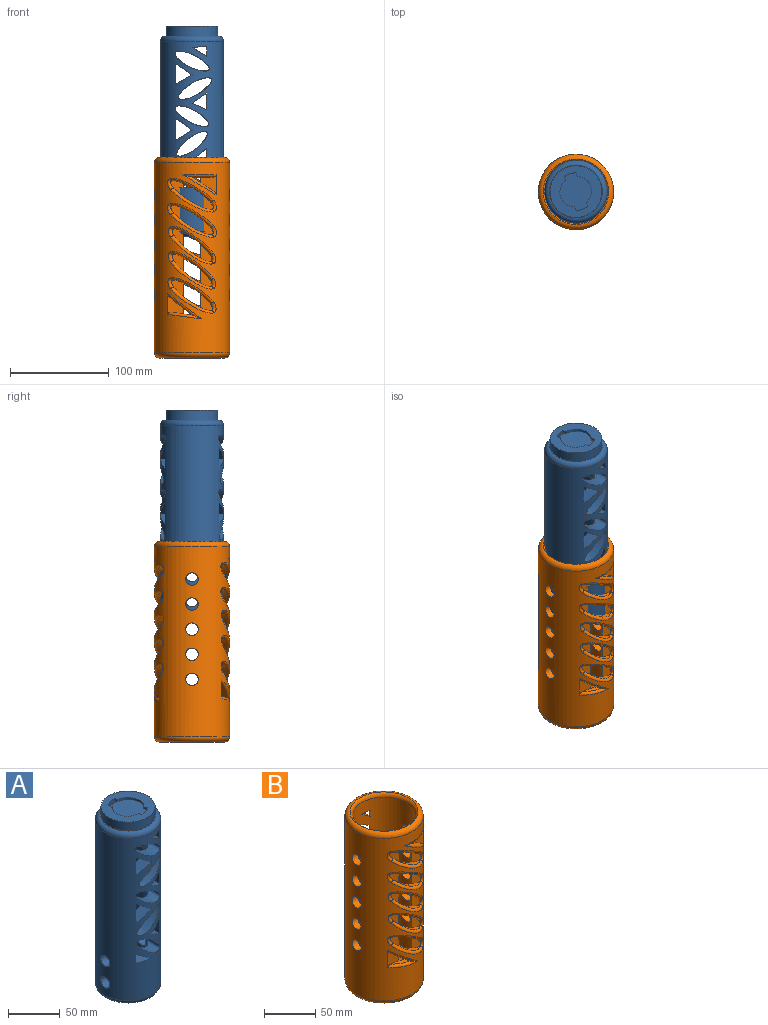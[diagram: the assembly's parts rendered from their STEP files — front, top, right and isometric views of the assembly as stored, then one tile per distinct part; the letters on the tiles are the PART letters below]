
ASSEMBLY  parts=2 mates=1
PART A: 68 faces, bbox 69x69x213.6 mm
  f0: cylinder r=31.75mm len=193.04mm, axis (0,0,-1), area 32342.8mm2, adj f4,f5,f6,f7,f8,f9,f10,f11
  f1: cylinder r=19.05mm len=203.2mm, axis (0,0,1), area 17379.8mm2, adj f3,f6,f7,f8,f9,f10,f11,f12
  f2: plane 53.34x53.34mm, normal (0,0,1), area 75.9mm2, adj f5,f56
  f3: plane 53.34x53.34mm, normal (0,0,-1), area 1094.5mm2, adj f1,f4
  f4: torus R=26.67mm, axis (0,0,1), area 1499.3mm2, adj f0,f3
  f5: torus R=26.67mm, axis (0,0,1), area 1499.3mm2, adj f0,f2
  f6: cylinder r=6.35mm len=13.79mm, axis (1,0,0), area 515.5mm2, adj f0,f1
  f7: cylinder r=6.35mm len=13.79mm, axis (1,0,0), area 515.5mm2, adj f0,f1
  f8: cylinder r=6.35mm len=13.79mm, axis (1,0,0), area 515.5mm2, adj f0,f1
  f9: cylinder r=6.35mm len=13.79mm, axis (1,0,0), area 515.5mm2, adj f0,f1
  f10: extruded ~31.64x24.69mm, area 1200.9mm2, adj f0,f1
  f11: extruded ~31.64x24.69mm, area 1200.7mm2, adj f0,f1
  f12: plane 22.21x16.49mm, normal (0,0,1), area 230.4mm2, adj f0,f1,f13,f14
  f13: plane 17.59x10.4mm, normal (1,0,0), area 182.9mm2, adj f0,f1,f12,f14
  f14: plane 22.21x16.49mm, normal (-0.53,0,-0.85), area 272.4mm2, adj f0,f1,f12,f13
  f15: plane 22.21x16.49mm, normal (-0.53,0,-0.85), area 272.4mm2, adj f0,f1,f16,f17
  f16: plane 17.59x10.4mm, normal (1,0,0), area 182.9mm2, adj f0,f1,f15,f17
  f17: plane 22.21x16.49mm, normal (0,0,1), area 230.4mm2, adj f0,f1,f15,f16
  f18: plane 19.93x14.94mm, normal (0.53,0,0.85), area 241.2mm2, adj f0,f1,f19,f20
  f19: plane 19.99x15mm, normal (0.03,0,-1), area 204.5mm2, adj f0,f1,f18,f20
  f20: plane 16.2x9.88mm, normal (-1,0,0), area 160mm2, adj f0,f1,f18,f19
  f21: plane 16.2x9.88mm, normal (-1,0,0), area 160mm2, adj f0,f1,f22,f23
  f22: plane 19.99x15mm, normal (0.03,0,-1), area 204.5mm2, adj f0,f1,f21,f23
  f23: plane 19.93x14.94mm, normal (0.53,0,0.85), area 241.2mm2, adj f0,f1,f21,f22
  f24: extruded ~31.09x25.36mm, area 1192.9mm2, adj f0,f1
  f25: extruded ~31.09x25.36mm, area 1192.9mm2, adj f0,f1
  f26: extruded ~33.98x23.15mm, area 1226.3mm2, adj f0,f1
  f27: extruded ~33.98x23.15mm, area 1226.7mm2, adj f0,f1
  f28: extruded ~63.5x33.44mm, area 2541.8mm2, adj f0,f1
  f29: extruded ~34.6x23.8mm, area 1230.5mm2, adj f0,f1
  f30: extruded ~34.6x23.8mm, area 1230.1mm2, adj f0,f1
  f31: plane 22.21x16.49mm, normal (-0.53,0,0.85), area 272mm2, adj f0,f1,f32,f33
  f32: plane 22.68x17.59mm, normal (1,0,0), area 398.9mm2, adj f0,f1,f31,f33
  f33: plane 22.21x16.49mm, normal (-0.6,0,-0.8), area 287.8mm2, adj f0,f1,f31,f32
  f34: plane 22.21x16.49mm, normal (-0.6,0,-0.8), area 287.8mm2, adj f0,f1,f35,f36
  f35: plane 22.68x17.59mm, normal (1,0,0), area 398.9mm2, adj f0,f1,f34,f36
  f36: plane 22.21x16.49mm, normal (-0.53,0,0.85), area 272mm2, adj f0,f1,f34,f35
  f37: plane 20.2x15.21mm, normal (0.49,0,0.87), area 234.2mm2, adj f0,f1,f38,f39
  f38: plane 19.93x14.94mm, normal (0.61,0,-0.79), area 258.2mm2, adj f0,f1,f37,f39
  f39: plane 19.89x16.2mm, normal (-1,0,0), area 322.2mm2, adj f0,f1,f37,f38
  f40: plane 19.89x16.2mm, normal (-1,0,0), area 322.2mm2, adj f0,f1,f41,f42
  f41: plane 19.93x14.94mm, normal (0.61,0,-0.79), area 258.2mm2, adj f0,f1,f40,f42
  f42: plane 20.2x15.21mm, normal (0.49,0,0.87), area 234.2mm2, adj f0,f1,f40,f41
  f43: plane 20.15x15.16mm, normal (0.41,0,0.91), area 224.3mm2, adj f0,f1,f44,f45
  f44: plane 19.93x14.94mm, normal (0.57,0,-0.82), area 248.6mm2, adj f0,f1,f43,f45
  f45: plane 17.11x16.2mm, normal (-1,0,0), area 277.1mm2, adj f0,f1,f43,f44
  f46: plane 17.11x16.2mm, normal (-1,0,0), area 277.1mm2, adj f0,f1,f47,f48
  f47: plane 19.93x14.94mm, normal (0.57,0,-0.82), area 248.6mm2, adj f0,f1,f46,f48
  f48: plane 20.15x15.16mm, normal (0.41,0,0.91), area 224.3mm2, adj f0,f1,f46,f47
  f49: plane 22.21x16.49mm, normal (-0.5,0,0.87), area 266.3mm2, adj f0,f1,f50,f51
  f50: plane 21.09x17.59mm, normal (1,0,0), area 371mm2, adj f0,f1,f49,f51
  f51: plane 22.21x16.49mm, normal (-0.57,0,-0.82), area 281.2mm2, adj f0,f1,f49,f50
  f52: plane 22.21x16.49mm, normal (-0.57,0,-0.82), area 281.2mm2, adj f0,f1,f53,f54
  f53: plane 21.09x17.59mm, normal (1,0,0), area 371mm2, adj f0,f1,f52,f54
  f54: plane 22.21x16.49mm, normal (-0.5,0,0.87), area 266.3mm2, adj f0,f1,f52,f53
  f55: plane 52.43x52.43mm, normal (0,0,1), area 1288mm2, adj f56,f58,f61,f62,f63,f65,f66,f67
  f56: cylinder r=26.21mm len=52.43mm, axis (0,0,-1), area 1673.4mm2, adj f2,f55
  f57: plane 38.1x38.1mm, normal (0,0,-1), area 1140.1mm2, adj f1
  f58: cylinder r=19.05mm len=38.1mm, axis (0,0,1), area 369.8mm2, adj f55,f59,f60,f61,f63,f64,f65,f66
  f59: plane 38.1x38.1mm, normal (0,0,1), area 1140.1mm2, adj f58
  f60: plane 33.87x19.05mm, normal (0,0,-1), area 145.3mm2, adj f58,f61,f62,f63
  f61: plane 3.59x2.54mm, normal (-0.94,-0.33,0), area 9.7mm2, adj f55,f58,f60,f62
  f62: cylinder r=15.49mm len=26.68mm, axis (0,0,1), area 90.7mm2, adj f55,f60,f61,f63
  f63: plane 3.59x2.54mm, normal (-0.94,-0.33,0), area 9.7mm2, adj f55,f58,f60,f62
  f64: plane 33.87x19.05mm, normal (0,0,-1), area 124.2mm2, adj f58,f65,f66,f67
  f65: plane 3.59x2.54mm, normal (0.94,0.33,0), area 9.7mm2, adj f55,f58,f64,f67
  f66: plane 3.59x2.54mm, normal (0.94,0.33,0), area 9.7mm2, adj f55,f58,f64,f67
  f67: cylinder r=14.97mm len=26.68mm, axis (0,0,1), area 94.2mm2, adj f55,f64,f65,f66
PART B: 129 faces, bbox 85x85x206.4 mm
  f0: extruded ~38.38x19.92mm, area 191.3mm2, adj f12,f50,f51,f123
  f1: extruded ~38.66x16.78mm, area 185.5mm2, adj f12,f61,f62,f119
  f2: extruded ~38.79x14.74mm, area 182.2mm2, adj f12,f64,f65,f115
  f3: extruded ~38.45x19.27mm, area 190mm2, adj f12,f67,f68,f111
  f4: extruded ~38.66x16.81mm, area 185.5mm2, adj f12,f70,f71,f107
  f5: extruded ~37.42x25.88mm, area 204mm2, adj f12,f32,f33,f100
  f6: extruded ~37.88x23.46mm, area 198.6mm2, adj f12,f35,f36,f96
  f7: extruded ~38.2x21.32mm, area 194.1mm2, adj f12,f41,f42,f90
  f8: extruded ~37.39x26.06mm, area 204.4mm2, adj f12,f44,f45,f86
  f9: extruded ~38.14x21.81mm, area 195.1mm2, adj f12,f47,f48,f82
  f10: cylinder r=25.4mm len=50.8mm, axis (0,0,-1), area 726mm2, adj f13,f72,f73,f75,f76,f77,f79,f80
  f11: cylinder r=38.1mm len=193.04mm, axis (0,0,-1), area 37391.9mm2, adj f15,f16,f18,f19,f20,f21,f22,f23
  f12: cylinder r=30.48mm len=173.4mm, axis (0,0,1), area 29441.8mm2, adj f0,f1,f2,f3,f4,f5,f6,f7
  f13: plane 66.04x66.04mm, normal (0,0,-1), area 1951.1mm2, adj f10,f16,f74,f75,f76,f78,f79,f80
  f14: cone r=0mm half-angle=59deg, axis (0,0,1), area 3402.1mm2, adj f12,f72
  f15: torus R=33.02mm, axis (0,0,1), area 1817.7mm2, adj f11,f17
  f16: torus R=33.02mm, axis (0,0,1), area 1817.7mm2, adj f11,f13
  f17: torus R=35.56mm, axis (0,0,1), area 1048.2mm2, adj f12,f15
  f18: cylinder r=6.35mm len=12.7mm, axis (1,0,0), area 304mm2, adj f11,f12
  f19: cylinder r=6.35mm len=12.7mm, axis (1,0,0), area 304mm2, adj f11,f12
  f20: cylinder r=6.35mm len=12.7mm, axis (1,0,0), area 304mm2, adj f11,f12
  f21: cylinder r=6.35mm len=12.7mm, axis (1,0,0), area 304mm2, adj f11,f12
  f22: cylinder r=6.35mm len=12.7mm, axis (1,0,0), area 304mm2, adj f11,f12
  f23: cylinder r=6.35mm len=12.7mm, axis (-1,0,0), area 304mm2, adj f11,f12
  f24: cylinder r=6.35mm len=12.7mm, axis (-1,0,0), area 304mm2, adj f11,f12
  f25: cylinder r=6.35mm len=12.7mm, axis (-1,0,0), area 304mm2, adj f11,f12
  f26: cylinder r=6.35mm len=12.7mm, axis (-1,0,0), area 304mm2, adj f11,f12
  f27: cylinder r=6.35mm len=12.7mm, axis (-1,0,0), area 304mm2, adj f11,f12
  f28: plane 20.28x6.35mm, normal (0,0,-1), area 80.1mm2, adj f12,f29,f30,f103,f104
  f29: plane 21.73x14.14mm, normal (0.54,0,0.84), area 106mm2, adj f12,f28,f30,f103
  f30: plane 21.62x16.97mm, normal (0,-1,0), area 173.1mm2, adj f11,f12,f28,f29,f103,f104
  f31: extruded ~37.42x25.88mm, area 204mm2, adj f12,f32,f33,f101
  f32: plane 18.06x12.2mm, normal (0,-1,0), area 119.5mm2, adj f5,f12,f31,f102
  f33: plane 18.06x12.2mm, normal (0,-1,0), area 119.5mm2, adj f5,f12,f31,f99
  f34: extruded ~37.88x23.46mm, area 198.6mm2, adj f12,f35,f36,f97
  f35: plane 17.85x13.3mm, normal (0,-1,0), area 124mm2, adj f6,f12,f34,f98
  f36: plane 17.85x13.3mm, normal (0,-1,0), area 124mm2, adj f6,f12,f34,f95
  f37: plane 19.94x6.36mm, normal (0.14,0,0.99), area 78.6mm2, adj f12,f38,f39,f93,f94
  f38: plane 21.94x17.47mm, normal (-0.62,0,-0.78), area 115.2mm2, adj f12,f37,f39,f93
  f39: plane 20.79x15.76mm, normal (0,-1,0), area 175.1mm2, adj f11,f12,f37,f38,f93,f94
  f40: extruded ~38.2x21.32mm, area 194.1mm2, adj f12,f41,f42,f91
  f41: plane 17.64x14.28mm, normal (0,-1,0), area 127.6mm2, adj f7,f12,f40,f92
  f42: plane 17.64x14.28mm, normal (0,-1,0), area 127.6mm2, adj f7,f12,f40,f89
  f43: extruded ~37.39x26.06mm, area 204.4mm2, adj f12,f44,f45,f87
  f44: plane 18.07x12.12mm, normal (0,-1,0), area 119.2mm2, adj f8,f12,f43,f88
  f45: plane 18.07x12.12mm, normal (0,-1,0), area 119.2mm2, adj f8,f12,f43,f85
  f46: extruded ~38.14x21.81mm, area 195.1mm2, adj f12,f47,f48,f83
  f47: plane 17.69x14.05mm, normal (0,-1,0), area 126.8mm2, adj f9,f12,f46,f84
  f48: plane 17.69x14.05mm, normal (0,-1,0), area 126.8mm2, adj f9,f12,f46,f81
  f49: extruded ~38.38x19.92mm, area 191.3mm2, adj f12,f50,f51,f122
  f50: plane 17.52x14.94mm, normal (0,1,0), area 129.8mm2, adj f0,f12,f49,f121
  f51: plane 17.52x14.94mm, normal (0,1,0), area 129.8mm2, adj f0,f12,f49,f124
  f52: plane 21.78x1.16mm, normal (-1,0,0), area 16.7mm2, adj f11,f55,f127,f128
  f53: plane 20.3x6.35mm, normal (0.01,0,-1), area 80.2mm2, adj f12,f54,f55,f127,f128
  f54: plane 21.83x15.68mm, normal (0.58,0,0.81), area 110.2mm2, adj f12,f53,f55,f127
  f55: plane 18.23x14.84mm, normal (0,1,0), area 171.6mm2, adj f12,f52,f53,f54,f127,f128
  f56: plane 19.5x4.12mm, normal (1,0,0), area 50.9mm2, adj f11,f57,f58,f59,f125,f126
  f57: plane 19.65x6.35mm, normal (0,0,1), area 80mm2, adj f12,f56,f58,f59,f125,f126
  f58: plane 19.71x14.16mm, normal (-0.58,0,-0.81), area 108.3mm2, adj f12,f56,f57,f59,f125
  f59: plane 14.1x10.94mm, normal (0,1,0), area 111.3mm2, adj f12,f56,f57,f58
  f60: extruded ~38.66x16.78mm, area 185.5mm2, adj f12,f61,f62,f118
  f61: plane 17.22x16.43mm, normal (0,1,0), area 134.2mm2, adj f1,f12,f60,f120
  f62: plane 17.22x16.43mm, normal (0,1,0), area 134.2mm2, adj f1,f12,f60,f117
  f63: extruded ~38.79x14.74mm, area 182.2mm2, adj f12,f64,f65,f114
  f64: plane 17.32x16.98mm, normal (0,1,0), area 136.7mm2, adj f2,f12,f63,f116
  f65: plane 17.32x16.98mm, normal (0,1,0), area 136.7mm2, adj f2,f12,f63,f113
  f66: extruded ~38.45x19.27mm, area 190mm2, adj f12,f67,f68,f110
  f67: plane 17.46x15.26mm, normal (0,1,0), area 130.8mm2, adj f3,f12,f66,f109
  f68: plane 17.46x15.26mm, normal (0,1,0), area 130.8mm2, adj f3,f12,f66,f112
  f69: extruded ~38.66x16.81mm, area 185.5mm2, adj f12,f70,f71,f106
  f70: plane 17.22x16.42mm, normal (0,1,0), area 134.2mm2, adj f4,f12,f69,f105
  f71: plane 17.22x16.42mm, normal (0,1,0), area 134.2mm2, adj f4,f12,f69,f108
  f72: plane 50.8x50.8mm, normal (0,0,-1), area 2024.3mm2, adj f10,f14
  f73: plane 48.46x17.78mm, normal (0,0,1), area 276.3mm2, adj f10,f74,f75,f76
  f74: cylinder r=20.52mm len=38.1mm, axis (0,0,-1), area 186.1mm2, adj f13,f73,f75,f76
  f75: plane 5.18x3.81mm, normal (0,-1,0), area 19.7mm2, adj f10,f13,f73,f74
  f76: plane 5.18x3.81mm, normal (0,-1,0), area 19.7mm2, adj f10,f13,f73,f74
  f77: plane 48.46x17.78mm, normal (0,0,1), area 276.3mm2, adj f10,f78,f79,f80
  f78: cylinder r=20.52mm len=38.1mm, axis (0,0,-1), area 186.1mm2, adj f13,f77,f79,f80
  f79: plane 5.18x3.81mm, normal (0,1,0), area 19.7mm2, adj f10,f13,f77,f78
  f80: plane 5.18x3.81mm, normal (0,1,0), area 19.7mm2, adj f10,f13,f77,f78
  f81: bspline ~12.6x6.83mm, area 44.1mm2, adj f11,f48,f82,f83
  f82: bspline ~45.59x26.87mm, area 209.1mm2, adj f9,f11,f81,f84
  f83: bspline ~44.72x26.76mm, area 209.1mm2, adj f11,f46,f81,f84
  f84: bspline ~12.6x6.83mm, area 44.1mm2, adj f11,f47,f82,f83
  f85: bspline ~11.11x6.02mm, area 40.3mm2, adj f11,f45,f86,f87
  f86: bspline ~44.08x30.23mm, area 220.5mm2, adj f8,f11,f85,f88
  f87: bspline ~44.08x30.59mm, area 220.5mm2, adj f11,f43,f85,f88
  f88: bspline ~11.11x6.02mm, area 40.3mm2, adj f11,f44,f86,f87
  f89: bspline ~12.67x6.87mm, area 44.3mm2, adj f11,f42,f90,f91
  f90: bspline ~45.44x25.9mm, area 208mm2, adj f7,f11,f89,f92
  f91: bspline ~44.64x25.95mm, area 208mm2, adj f11,f40,f89,f92
  f92: bspline ~12.67x6.87mm, area 44.3mm2, adj f11,f41,f90,f91
  f93: bspline ~40.08x31.83mm, area 127.2mm2, adj f11,f37,f38,f39,f94
  f94: bspline ~39.89x14.07mm, area 121mm2, adj f11,f37,f39,f93
  f95: bspline ~11.8x6.29mm, area 43.2mm2, adj f11,f36,f96,f97
  f96: bspline ~44.45x28mm, area 213.3mm2, adj f6,f11,f95,f98
  f97: bspline ~44.43x27.99mm, area 213.3mm2, adj f11,f34,f95,f98
  f98: bspline ~11.8x6.29mm, area 43.2mm2, adj f11,f35,f96,f97
  f99: bspline ~11.52x6.3mm, area 40.6mm2, adj f11,f33,f100,f101
  f100: bspline ~44.01x30.09mm, area 220mm2, adj f5,f11,f99,f102
  f101: bspline ~44.44x30.42mm, area 220mm2, adj f11,f31,f99,f102
  f102: bspline ~11.52x6.3mm, area 40.6mm2, adj f11,f32,f100,f101
  f103: bspline ~40.04x26.55mm, area 120.4mm2, adj f11,f28,f29,f30,f104
  f104: torus R=35.56mm, axis (0,0,-1), area 115.1mm2, adj f11,f28,f30,f103
  f105: bspline ~13.09x7.02mm, area 43.4mm2, adj f11,f70,f106,f107
  f106: bspline ~45.5x21.74mm, area 198.6mm2, adj f11,f69,f105,f108
  f107: bspline ~44.71x21.22mm, area 198.6mm2, adj f4,f11,f105,f108
  f108: bspline ~13.09x7.02mm, area 43.4mm2, adj f11,f71,f106,f107
  f109: bspline ~12.37x6.48mm, area 44.3mm2, adj f11,f67,f110,f111
  f110: bspline ~45.67x23.7mm, area 203.4mm2, adj f11,f66,f109,f112
  f111: bspline ~44.72x23.64mm, area 203.4mm2, adj f3,f11,f109,f112
  f112: bspline ~12.37x6.48mm, area 44.3mm2, adj f11,f68,f110,f111
  f113: bspline ~13.19x6.97mm, area 41.9mm2, adj f11,f65,f114,f115
  f114: bspline ~45.47x19.4mm, area 195.1mm2, adj f11,f63,f113,f116
  f115: bspline ~45.91x18.9mm, area 195.1mm2, adj f2,f11,f113,f116
  f116: bspline ~13.19x6.97mm, area 41.9mm2, adj f11,f64,f114,f115
  f117: bspline ~13.1x7.02mm, area 43.3mm2, adj f11,f62,f118,f119
  f118: bspline ~45.36x21.88mm, area 198.6mm2, adj f11,f60,f117,f120
  f119: bspline ~44.69x21.12mm, area 198.6mm2, adj f1,f11,f117,f120
  f120: bspline ~13.1x7.02mm, area 43.3mm2, adj f11,f61,f118,f119
  f121: bspline ~12.84x6.95mm, area 44.4mm2, adj f11,f50,f122,f123
  f122: bspline ~44.85x24.5mm, area 204.9mm2, adj f11,f49,f121,f124
  f123: bspline ~43.46x22.63mm, area 204.9mm2, adj f0,f11,f121,f124
  f124: bspline ~12.84x6.95mm, area 44.4mm2, adj f11,f51,f122,f123
  f125: bspline ~36.61x26.58mm, area 104.7mm2, adj f11,f56,f57,f58,f126
  f126: torus R=35.56mm, axis (0,0,-1), area 100.4mm2, adj f11,f56,f57,f125
  f127: bspline ~40.06x29mm, area 119.7mm2, adj f11,f52,f53,f54,f55,f128
  f128: bspline ~39.59x14.05mm, area 113.6mm2, adj f11,f52,f53,f55,f127
PLACE A t=(-3.97,-0.43,30.29)mm
PLACE B t=(-3.97,-0.43,-92.78)mm
MATE slider B.f12 <-> A.f0  axis (0,0,1) through (-3.97,-0.43,106.02)mm
